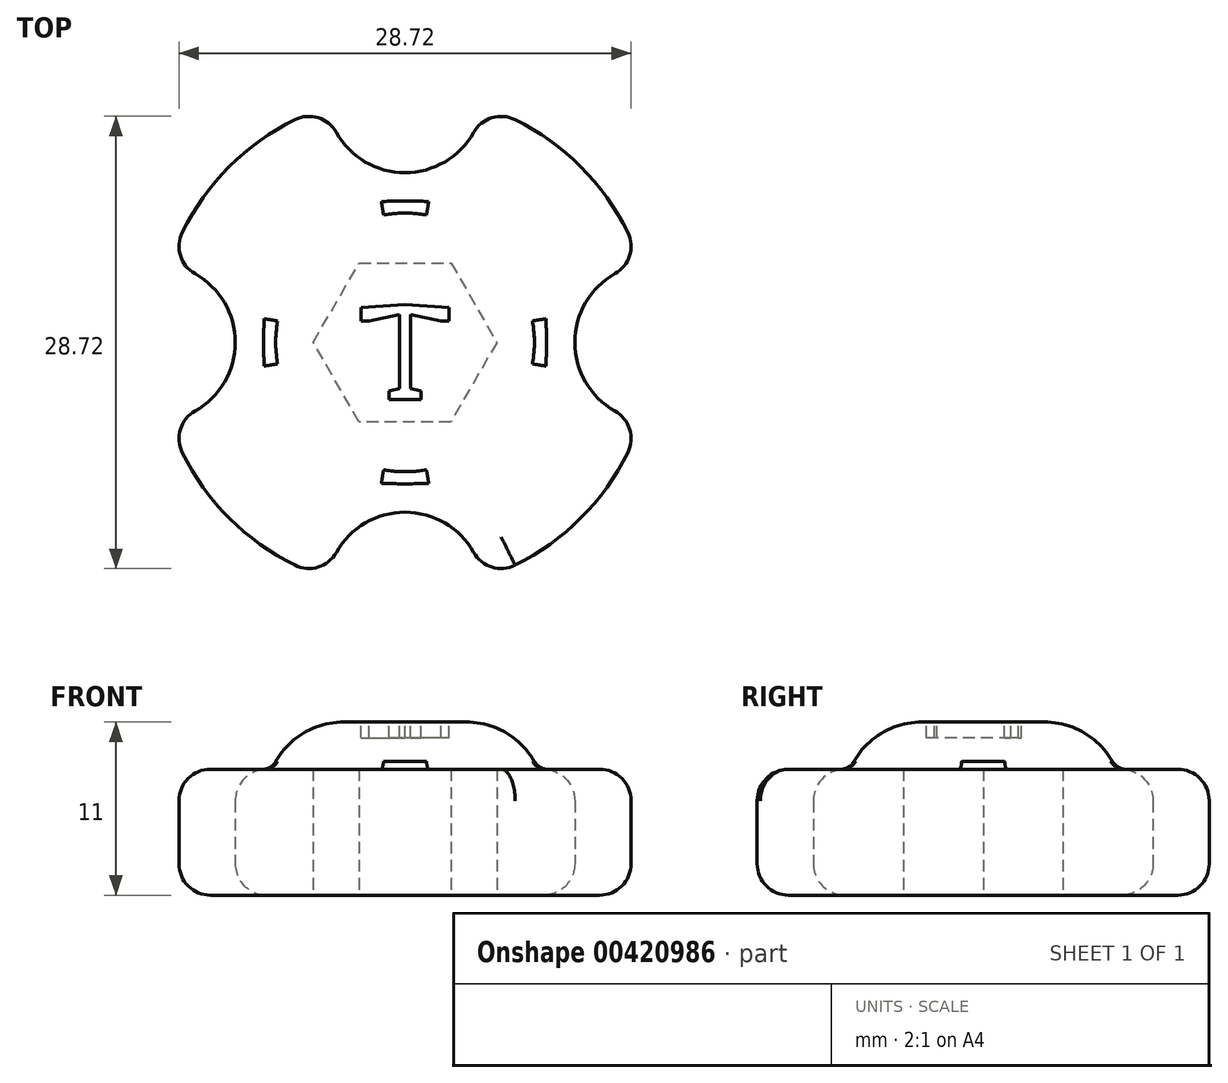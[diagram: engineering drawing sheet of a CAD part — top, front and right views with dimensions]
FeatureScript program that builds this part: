
annotation { "Feature Type Name" : "Feature", "Feature Type Description" : "" }
export const myFeature = defineFeature(function(context is Context, id is Id, definition is map)
    precondition{}
    {
        {
            var Q0;
            Q0=qCreatedBy(makeId("Top.planeOp"),FACE);
            var sketch = newSketch(context, id + "F0", { "sketchPlane" : qUnion([Q0])});
            skLineSegment(sketch, "E0.0", {"start": v(-2.92, 5.05) * mm, "end": v(2.92, 5.05) * mm});
            skLineSegment(sketch, "E0.1", {"start": v(2.92, 5.05) * mm, "end": v(5.83, 0) * mm});
            skLineSegment(sketch, "E0.2", {"start": v(5.83, 0) * mm, "end": v(2.92, -5.05) * mm});
            skLineSegment(sketch, "E0.3", {"start": v(2.92, -5.05) * mm, "end": v(-2.92, -5.05) * mm});
            skLineSegment(sketch, "E0.4", {"start": v(-2.92, -5.05) * mm, "end": v(-5.83, 0) * mm});
            skLineSegment(sketch, "E0.5", {"start": v(-5.83, 0) * mm, "end": v(-2.92, 5.05) * mm});
            skPoint(sketch, "E0.0.midPoint", {"position": v(0, 5.05) * mm});
            skArc(sketch, "E1", {"start": v(-7, 14.15) * mm, "mid": v(-11.16, 11.16) * mm, "end": v(-14.15, 7) * mm});
            skArc(sketch, "E2", {"start": v(-4.36, 13.34) * mm, "mid": v(0, 10.78) * mm, "end": v(4.36, 13.34) * mm});
            skArc(sketch, "E3", {"start": v(-13.34, -4.36) * mm, "mid": v(-10.78, 0) * mm, "end": v(-13.34, 4.36) * mm});
            skArc(sketch, "E4", {"start": v(4.36, -13.34) * mm, "mid": v(0, -10.78) * mm, "end": v(-4.36, -13.34) * mm});
            skArc(sketch, "E5", {"start": v(13.34, 4.36) * mm, "mid": v(10.78, 0) * mm, "end": v(13.34, -4.36) * mm});
            skArc(sketch, "E6.trimOffspring", {"start": v(-14.15, -7) * mm, "mid": v(-11.16, -11.16) * mm, "end": v(-7, -14.15) * mm});
            skArc(sketch, "E7.trimOffspring", {"start": v(7, -14.15) * mm, "mid": v(11.16, -11.16) * mm, "end": v(14.15, -7) * mm});
            skArc(sketch, "E8.trimOffspring", {"start": v(14.15, 7) * mm, "mid": v(11.16, 11.16) * mm, "end": v(7, 14.15) * mm});
            skPoint(sketch, "E9.visualSharp", {"position": v(-4.94, 15) * mm});
            skArc(sketch, "E9.filletArc", {"start": v(-4.36, 13.34) * mm, "mid": v(-5.51, 14.27) * mm, "end": v(-7, 14.15) * mm});
            skPoint(sketch, "E10.visualSharp", {"position": v(-15, 4.94) * mm});
            skArc(sketch, "E10.filletArc", {"start": v(-14.15, 7) * mm, "mid": v(-14.27, 5.51) * mm, "end": v(-13.34, 4.36) * mm});
            skPoint(sketch, "E11.visualSharp", {"position": v(-15, -4.94) * mm});
            skArc(sketch, "E11.filletArc", {"start": v(-13.34, -4.36) * mm, "mid": v(-14.27, -5.51) * mm, "end": v(-14.15, -7) * mm});
            skPoint(sketch, "E12.visualSharp", {"position": v(-4.94, -15) * mm});
            skArc(sketch, "E12.filletArc", {"start": v(-7, -14.15) * mm, "mid": v(-5.51, -14.27) * mm, "end": v(-4.36, -13.34) * mm});
            skPoint(sketch, "E13.visualSharp", {"position": v(4.94, -15) * mm});
            skArc(sketch, "E13.filletArc", {"start": v(4.36, -13.34) * mm, "mid": v(5.51, -14.27) * mm, "end": v(7, -14.15) * mm});
            skPoint(sketch, "E14.visualSharp", {"position": v(15, -4.94) * mm});
            skArc(sketch, "E14.filletArc", {"start": v(14.15, -7) * mm, "mid": v(14.27, -5.51) * mm, "end": v(13.34, -4.36) * mm});
            skPoint(sketch, "E15.visualSharp", {"position": v(4.94, 15) * mm});
            skArc(sketch, "E15.filletArc", {"start": v(7, 14.15) * mm, "mid": v(5.51, 14.27) * mm, "end": v(4.36, 13.34) * mm});
            skPoint(sketch, "E16.visualSharp", {"position": v(15, 4.94) * mm});
            skArc(sketch, "E16.filletArc", {"start": v(13.34, 4.36) * mm, "mid": v(14.27, 5.51) * mm, "end": v(14.15, 7) * mm});
            skSolve(sketch);
        }
        {
            var Q0;
            Q0 = qSketchRegion(id + "F0", true);
            extrude(context, id + "F1", {"entities" : qUnion([Q0]), "depth" : 8 * mm, "offsetDistance" : 25 * mm});
        }
        {
            var Q0;
            Q0=makeQuery(id+"F1.opExtrude","CAP_EDGE",EDGE,{"disambiguationData":[OSD([sQuery(id+"F0.wireOp",EDGE,"E8.trimOffspring")])],"isStart":false});
            var Q1;
            Q1=makeQuery(id+"F1.opExtrude","CAP_EDGE",EDGE,{"disambiguationData":[OSD([sQuery(id+"F0.wireOp",EDGE,"E2")])],"isStart":false});
            var Q2;
            Q2=makeQuery(id+"F1.opExtrude","CAP_EDGE",EDGE,{"disambiguationData":[OSD([sQuery(id+"F0.wireOp",EDGE,"E15.filletArc")])],"isStart":false});
            var Q3;
            Q3=makeQuery(id+"F1.opExtrude","CAP_EDGE",EDGE,{"disambiguationData":[OSD([sQuery(id+"F0.wireOp",EDGE,"E9.filletArc")])],"isStart":false});
            var Q4;
            Q4=makeQuery(id+"F1.opExtrude","CAP_EDGE",EDGE,{"disambiguationData":[OSD([sQuery(id+"F0.wireOp",EDGE,"E1")])],"isStart":false});
            var Q5;
            Q5=makeQuery(id+"F1.opExtrude","CAP_EDGE",EDGE,{"disambiguationData":[OSD([sQuery(id+"F0.wireOp",EDGE,"E10.filletArc")])],"isStart":false});
            var Q6;
            Q6=makeQuery(id+"F1.opExtrude","CAP_EDGE",EDGE,{"disambiguationData":[OSD([sQuery(id+"F0.wireOp",EDGE,"E3")])],"isStart":false});
            var Q7;
            Q7=makeQuery(id+"F1.opExtrude","CAP_EDGE",EDGE,{"disambiguationData":[OSD([sQuery(id+"F0.wireOp",EDGE,"E16.filletArc")])],"isStart":false});
            var Q8;
            Q8=makeQuery(id+"F1.opExtrude","CAP_EDGE",EDGE,{"disambiguationData":[OSD([sQuery(id+"F0.wireOp",EDGE,"E5")])],"isStart":false});
            var Q9;
            Q9=makeQuery(id+"F1.opExtrude","CAP_EDGE",EDGE,{"disambiguationData":[OSD([sQuery(id+"F0.wireOp",EDGE,"E14.filletArc")])],"isStart":false});
            var Q10;
            Q10=makeQuery(id+"F1.opExtrude","CAP_EDGE",EDGE,{"disambiguationData":[OSD([sQuery(id+"F0.wireOp",EDGE,"E7.trimOffspring")])],"isStart":false});
            var Q11;
            Q11=makeQuery(id+"F1.opExtrude","CAP_EDGE",EDGE,{"disambiguationData":[OSD([sQuery(id+"F0.wireOp",EDGE,"E11.filletArc")])],"isStart":false});
            var Q12;
            Q12=makeQuery(id+"F1.opExtrude","CAP_EDGE",EDGE,{"disambiguationData":[OSD([sQuery(id+"F0.wireOp",EDGE,"E6.trimOffspring")])],"isStart":false});
            var Q13;
            Q13=makeQuery(id+"F1.opExtrude","CAP_EDGE",EDGE,{"disambiguationData":[OSD([sQuery(id+"F0.wireOp",EDGE,"E4")])],"isStart":false});
            var Q14;
            Q14=makeQuery(id+"F1.opExtrude","CAP_EDGE",EDGE,{"disambiguationData":[OSD([sQuery(id+"F0.wireOp",EDGE,"E12.filletArc")])],"isStart":false});
            var Q15;
            Q15=makeQuery(id+"F1.opExtrude","CAP_EDGE",EDGE,{"disambiguationData":[OSD([sQuery(id+"F0.wireOp",EDGE,"E13.filletArc")])],"isStart":false});
            fillet(context, id + "F2", {"entities" : qUnion([Q0, Q1, Q2, Q3, Q4, Q5, Q6, Q7, Q8, Q9, Q10, Q11, Q12, Q13, Q14, Q15]), "radius" : 2 * mm, "tangentPropagation" : true, "allowEdgeOverflow" : false});
        }
        {
            var Q0;
            Q0=makeQuery(id+"F1.opExtrude","CAP_EDGE",EDGE,{"disambiguationData":[OSD([sQuery(id+"F0.wireOp",EDGE,"E8.trimOffspring")])],"isStart":true});
            var Q1;
            Q1=makeQuery(id+"F1.opExtrude","CAP_EDGE",EDGE,{"disambiguationData":[OSD([sQuery(id+"F0.wireOp",EDGE,"E16.filletArc")])],"isStart":true});
            var Q2;
            Q2=makeQuery(id+"F1.opExtrude","CAP_EDGE",EDGE,{"disambiguationData":[OSD([sQuery(id+"F0.wireOp",EDGE,"E5")])],"isStart":true});
            var Q3;
            Q3=makeQuery(id+"F1.opExtrude","CAP_EDGE",EDGE,{"disambiguationData":[OSD([sQuery(id+"F0.wireOp",EDGE,"E14.filletArc")])],"isStart":true});
            var Q4;
            Q4=makeQuery(id+"F1.opExtrude","CAP_EDGE",EDGE,{"disambiguationData":[OSD([sQuery(id+"F0.wireOp",EDGE,"E7.trimOffspring")])],"isStart":true});
            var Q5;
            Q5=makeQuery(id+"F1.opExtrude","CAP_EDGE",EDGE,{"disambiguationData":[OSD([sQuery(id+"F0.wireOp",EDGE,"E13.filletArc")])],"isStart":true});
            var Q6;
            Q6=makeQuery(id+"F1.opExtrude","CAP_EDGE",EDGE,{"disambiguationData":[OSD([sQuery(id+"F0.wireOp",EDGE,"E4")])],"isStart":true});
            var Q7;
            Q7=makeQuery(id+"F1.opExtrude","CAP_EDGE",EDGE,{"disambiguationData":[OSD([sQuery(id+"F0.wireOp",EDGE,"E12.filletArc")])],"isStart":true});
            var Q8;
            Q8=makeQuery(id+"F1.opExtrude","CAP_EDGE",EDGE,{"disambiguationData":[OSD([sQuery(id+"F0.wireOp",EDGE,"E6.trimOffspring")])],"isStart":true});
            var Q9;
            Q9=makeQuery(id+"F1.opExtrude","CAP_EDGE",EDGE,{"disambiguationData":[OSD([sQuery(id+"F0.wireOp",EDGE,"E11.filletArc")])],"isStart":true});
            var Q10;
            Q10=makeQuery(id+"F1.opExtrude","CAP_EDGE",EDGE,{"disambiguationData":[OSD([sQuery(id+"F0.wireOp",EDGE,"E3")])],"isStart":true});
            var Q11;
            Q11=makeQuery(id+"F1.opExtrude","CAP_EDGE",EDGE,{"disambiguationData":[OSD([sQuery(id+"F0.wireOp",EDGE,"E10.filletArc")])],"isStart":true});
            var Q12;
            Q12=makeQuery(id+"F1.opExtrude","CAP_EDGE",EDGE,{"disambiguationData":[OSD([sQuery(id+"F0.wireOp",EDGE,"E1")])],"isStart":true});
            var Q13;
            Q13=makeQuery(id+"F1.opExtrude","CAP_EDGE",EDGE,{"disambiguationData":[OSD([sQuery(id+"F0.wireOp",EDGE,"E9.filletArc")])],"isStart":true});
            var Q14;
            Q14=makeQuery(id+"F1.opExtrude","CAP_EDGE",EDGE,{"disambiguationData":[OSD([sQuery(id+"F0.wireOp",EDGE,"E2")])],"isStart":true});
            var Q15;
            Q15=makeQuery(id+"F1.opExtrude","CAP_EDGE",EDGE,{"disambiguationData":[OSD([sQuery(id+"F0.wireOp",EDGE,"E15.filletArc")])],"isStart":true});
            fillet(context, id + "F3", {"entities" : qUnion([Q0, Q1, Q2, Q3, Q4, Q5, Q6, Q7, Q8, Q9, Q10, Q11, Q12, Q13, Q14, Q15]), "radius" : 2 * mm, "tangentPropagation" : true, "allowEdgeOverflow" : false});
        }
        {
            var Q0;
            Q0=makeQuery(id+"F1.opExtrude","CAP_FACE",FACE,{"disambiguationData":[OSD([sQuery(id+"F0.wireOp",EDGE,"E0.0"),sQuery(id+"F0.wireOp",EDGE,"E0.1"),sQuery(id+"F0.wireOp",EDGE,"E0.2"),sQuery(id+"F0.wireOp",EDGE,"E0.3"),sQuery(id+"F0.wireOp",EDGE,"E0.4"),sQuery(id+"F0.wireOp",EDGE,"E0.5"),sQuery(id+"F0.wireOp",EDGE,"E1"),sQuery(id+"F0.wireOp",EDGE,"E2"),sQuery(id+"F0.wireOp",EDGE,"E3"),sQuery(id+"F0.wireOp",EDGE,"E4"),sQuery(id+"F0.wireOp",EDGE,"E5"),sQuery(id+"F0.wireOp",EDGE,"E6.trimOffspring"),sQuery(id+"F0.wireOp",EDGE,"E7.trimOffspring"),sQuery(id+"F0.wireOp",EDGE,"E8.trimOffspring"),sQuery(id+"F0.wireOp",EDGE,"E9.filletArc"),sQuery(id+"F0.wireOp",EDGE,"E10.filletArc"),sQuery(id+"F0.wireOp",EDGE,"E11.filletArc"),sQuery(id+"F0.wireOp",EDGE,"E12.filletArc"),sQuery(id+"F0.wireOp",EDGE,"E13.filletArc"),sQuery(id+"F0.wireOp",EDGE,"E14.filletArc"),sQuery(id+"F0.wireOp",EDGE,"E15.filletArc"),sQuery(id+"F0.wireOp",EDGE,"E16.filletArc")])],"isStart":false});
            var sketch = newSketch(context, id + "F4", { "sketchPlane" : qUnion([Q0])});
            skCircle(sketch, "E17", {"center": v(0, 0) * mm, "radius": 8.46 * mm});
            skSolve(sketch);
        }
        {
            var Q0;
            Q0 = qSketchRegion(id + "F4", true);
            extrude(context, id + "F5", {"entities" : qUnion([Q0]), "operationType" : NewBodyOperationType.ADD, "depth" : 3 * mm, "offsetDistance" : 25 * mm});
        }
        {
            var Q0;
            Q0=makeQuery(id+"F5.opExtrude","CAP_EDGE",EDGE,{"disambiguationData":[OSD([sQuery(id+"F4.wireOp",EDGE,"E17")])],"isStart":false});
            fillet(context, id + "F6", {"entities" : qUnion([Q0]), "radius" : 5 * mm, "tangentPropagation" : true, "allowEdgeOverflow" : false});
        }
        {
            var Q0;
            Q0=makeQuery(id+"F6.opFillet","BLEND_EDGE",EDGE,{"blendedFrom":[makeQuery(id+"F5.opExtrude","CAP_EDGE",EDGE,{"disambiguationData":[OSD([sQuery(id+"F4.wireOp",EDGE,"E17")])],"isStart":false}),makeQuery(id+"F1.opExtrude","CAP_FACE",FACE,{"disambiguationData":[OSD([sQuery(id+"F0.wireOp",EDGE,"E0.0"),sQuery(id+"F0.wireOp",EDGE,"E0.1"),sQuery(id+"F0.wireOp",EDGE,"E0.2"),sQuery(id+"F0.wireOp",EDGE,"E0.3"),sQuery(id+"F0.wireOp",EDGE,"E0.4"),sQuery(id+"F0.wireOp",EDGE,"E0.5"),sQuery(id+"F0.wireOp",EDGE,"E1"),sQuery(id+"F0.wireOp",EDGE,"E2"),sQuery(id+"F0.wireOp",EDGE,"E3"),sQuery(id+"F0.wireOp",EDGE,"E4"),sQuery(id+"F0.wireOp",EDGE,"E5"),sQuery(id+"F0.wireOp",EDGE,"E6.trimOffspring"),sQuery(id+"F0.wireOp",EDGE,"E7.trimOffspring"),sQuery(id+"F0.wireOp",EDGE,"E8.trimOffspring"),sQuery(id+"F0.wireOp",EDGE,"E9.filletArc"),sQuery(id+"F0.wireOp",EDGE,"E10.filletArc"),sQuery(id+"F0.wireOp",EDGE,"E11.filletArc"),sQuery(id+"F0.wireOp",EDGE,"E12.filletArc"),sQuery(id+"F0.wireOp",EDGE,"E13.filletArc"),sQuery(id+"F0.wireOp",EDGE,"E14.filletArc"),sQuery(id+"F0.wireOp",EDGE,"E15.filletArc"),sQuery(id+"F0.wireOp",EDGE,"E16.filletArc")])],"isStart":false})],"blendedInto":[makeQuery(id+"F1.opExtrude","CAP_FACE",FACE,{"disambiguationData":[OSD([sQuery(id+"F0.wireOp",EDGE,"E0.0"),sQuery(id+"F0.wireOp",EDGE,"E0.1"),sQuery(id+"F0.wireOp",EDGE,"E0.2"),sQuery(id+"F0.wireOp",EDGE,"E0.3"),sQuery(id+"F0.wireOp",EDGE,"E0.4"),sQuery(id+"F0.wireOp",EDGE,"E0.5"),sQuery(id+"F0.wireOp",EDGE,"E1"),sQuery(id+"F0.wireOp",EDGE,"E2"),sQuery(id+"F0.wireOp",EDGE,"E3"),sQuery(id+"F0.wireOp",EDGE,"E4"),sQuery(id+"F0.wireOp",EDGE,"E5"),sQuery(id+"F0.wireOp",EDGE,"E6.trimOffspring"),sQuery(id+"F0.wireOp",EDGE,"E7.trimOffspring"),sQuery(id+"F0.wireOp",EDGE,"E8.trimOffspring"),sQuery(id+"F0.wireOp",EDGE,"E9.filletArc"),sQuery(id+"F0.wireOp",EDGE,"E10.filletArc"),sQuery(id+"F0.wireOp",EDGE,"E11.filletArc"),sQuery(id+"F0.wireOp",EDGE,"E12.filletArc"),sQuery(id+"F0.wireOp",EDGE,"E13.filletArc"),sQuery(id+"F0.wireOp",EDGE,"E14.filletArc"),sQuery(id+"F0.wireOp",EDGE,"E15.filletArc"),sQuery(id+"F0.wireOp",EDGE,"E16.filletArc")])],"isStart":false})]});
            fillet(context, id + "F7", {"entities" : qUnion([Q0]), "radius" : 1 * mm, "tangentPropagation" : true, "allowEdgeOverflow" : false});
        }
        {
            var Q0;
            Q0=makeQuery(id+"F5.opExtrude","CAP_FACE",FACE,{"disambiguationData":[OSD([sQuery(id+"F4.wireOp",EDGE,"E17")])],"isStart":false});
            var sketch = newSketch(context, id + "F8", { "sketchPlane" : qUnion([Q0])});
            skLineSegment(sketch, "E18.top", {"start": v(0, -3.61) * mm, "end": v(-1.01, -3.61) * mm});
            skLineSegment(sketch, "E18.right", {"start": v(-2.78, 2.23) * mm, "end": v(-2.78, 1.35) * mm});
            skLineSegment(sketch, "E19", {"start": v(-2.78, 2.23) * mm, "end": v(0, 2.41) * mm});
            skLineSegment(sketch, "E20", {"start": v(-2.78, 1.35) * mm, "end": v(-2.27, 1.35) * mm});
            skLineSegment(sketch, "E21", {"start": v(-2.27, 1.35) * mm, "end": v(-0.34, 1.77) * mm});
            skLineSegment(sketch, "E22", {"start": v(-0.34, 1.77) * mm, "end": v(-0.34, -2.94) * mm});
            skLineSegment(sketch, "E23", {"start": v(-0.34, -2.94) * mm, "end": v(-1.01, -3.1) * mm});
            skLineSegment(sketch, "E24", {"start": v(-1.01, -3.1) * mm, "end": v(-1.01, -3.61) * mm});
            skPoint(sketch, "E25.orphan", {"position": v(0, 3.53) * mm});
            skLineSegment(sketch, "E26.MirrorCS", {"start": v(2.78, 2.23) * mm, "end": v(0, 2.41) * mm});
            skLineSegment(sketch, "E27.MirrorCS", {"start": v(2.78, 2.23) * mm, "end": v(2.78, 1.35) * mm});
            skLineSegment(sketch, "E28.MirrorCS", {"start": v(2.78, 1.35) * mm, "end": v(2.27, 1.35) * mm});
            skLineSegment(sketch, "E29.MirrorCS", {"start": v(2.27, 1.35) * mm, "end": v(0.34, 1.77) * mm});
            skLineSegment(sketch, "E30.MirrorCS", {"start": v(0.34, 1.77) * mm, "end": v(0.34, -2.94) * mm});
            skLineSegment(sketch, "E31.MirrorCS", {"start": v(0.34, -2.94) * mm, "end": v(1.01, -3.1) * mm});
            skLineSegment(sketch, "E32.MirrorCS", {"start": v(1.01, -3.1) * mm, "end": v(1.01, -3.61) * mm});
            skLineSegment(sketch, "E33.MirrorCS", {"start": v(0, -3.61) * mm, "end": v(1.01, -3.61) * mm});
            skSolve(sketch);
        }
        {
            var Q0;
            Q0 = qSketchRegion(id + "F8", true);
            extrude(context, id + "F9", {"entities" : qUnion([Q0]), "operationType" : NewBodyOperationType.REMOVE, "oppositeDirection" : true, "depth" : 1 * mm, "offsetDistance" : 25 * mm});
        }
    });
